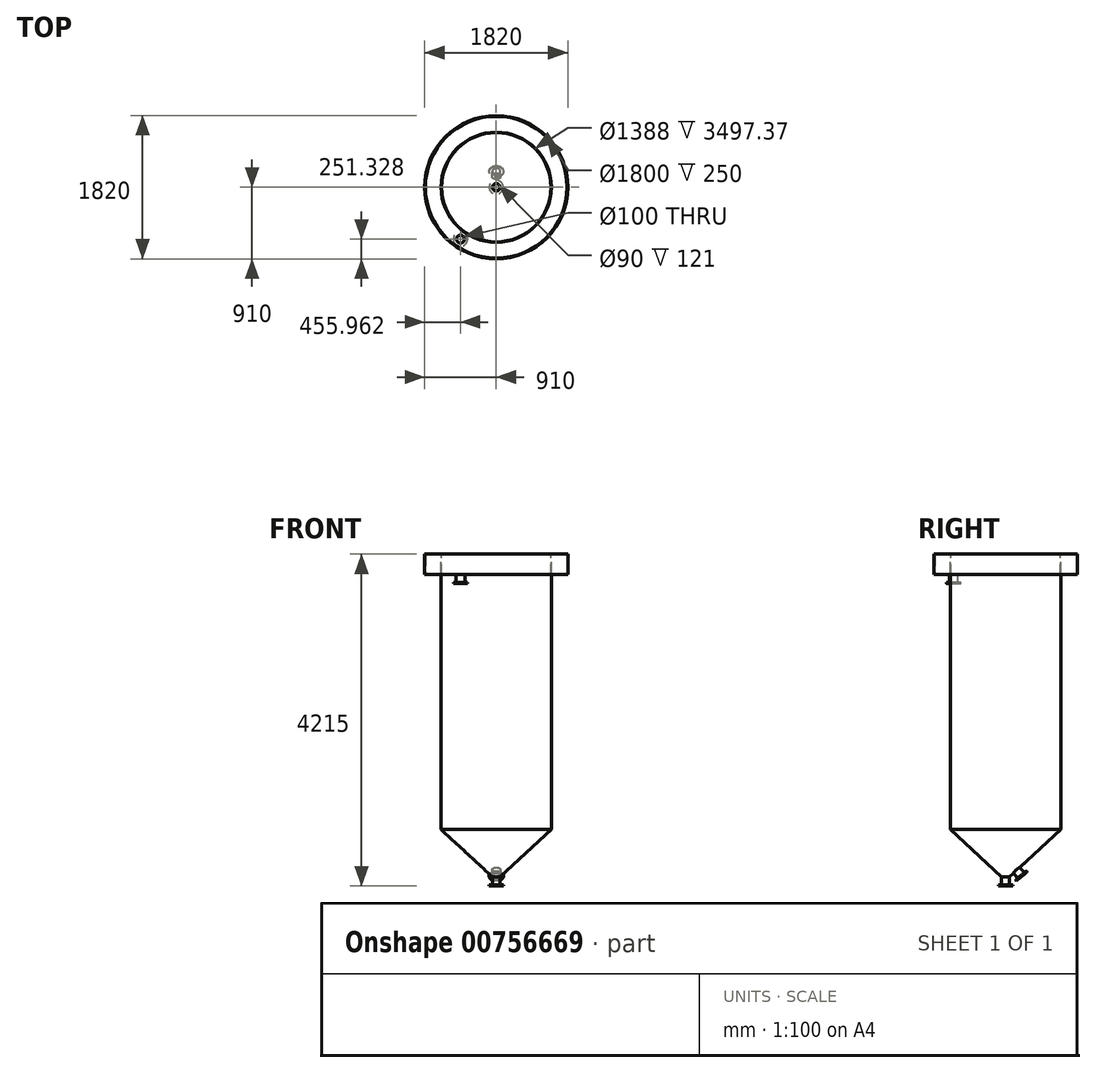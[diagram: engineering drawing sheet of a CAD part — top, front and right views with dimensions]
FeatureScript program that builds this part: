
annotation { "Feature Type Name" : "Feature", "Feature Type Description" : "" }
export const myFeature = defineFeature(function(context is Context, id is Id, definition is map)
    precondition{}
    {
        {
            var Q0;
            Q0=qCreatedBy(makeId("Top.planeOp"),FACE);
            var sketch = newSketch(context, id + "F0", { "sketchPlane" : qUnion([Q0])});
            skCircle(sketch, "E0", {"center": v(0, 0) * mm, "radius": 700 * mm});
            skSolve(sketch);
        }
        {
            var Q0;
            Q0 = qSketchRegion(id + "F0", true);
            extrude(context, id + "F1", {"entities" : qUnion([Q0]), "oppositeDirection" : true, "depth" : 3500 * mm, "offsetDistance" : 25 * mm});
        }
        {
            var Q0;
            Q0=makeQuery(id+"F1.opExtrude","CAP_FACE",FACE,{"disambiguationData":[OSD([sQuery(id+"F0.wireOp",EDGE,"E0")])],"isStart":false});
            var sketch = newSketch(context, id + "F2", { "sketchPlane" : qUnion([Q0])});
            skCircle(sketch, "E1", {"center": v(0, 0) * mm, "radius": 700 * mm});
            skSolve(sketch);
        }
        {
            var Q0;
            Q0 = qSketchRegion(id + "F2", true);
            extrude(context, id + "F3", {"entities" : qUnion([Q0]), "operationType" : NewBodyOperationType.ADD, "depth" : 600 * mm, "offsetDistance" : 25 * mm, "hasDraft" : true, "draftAngle" : 47.3 * degree, "draftPullDirection" : true});
        }
        {
            var Q0;
            Q0=makeQuery(id+"F1.opExtrude","CAP_FACE",FACE,{"disambiguationData":[OSD([sQuery(id+"F0.wireOp",EDGE,"E0")])],"isStart":true});
            shell(context, id + "F4", {"entities" : qUnion([Q0]), "thickness" : 6 * mm});
        }
        {
            var Q0;
            Q0=qCreatedBy(makeId("Front.planeOp"),FACE);
            var sketch = newSketch(context, id + "F5", { "sketchPlane" : qUnion([Q0])});
            skLineSegment(sketch, "E2", {"start": v(0, 0) * mm, "end": v(-700, 0) * mm, "construction": true});
            skLineSegment(sketch, "E3", {"start": v(-700, 0) * mm, "end": v(-700, -250) * mm, "construction": true});
            skLineSegment(sketch, "E4", {"start": v(-700, -250) * mm, "end": v(-700, -260) * mm});
            skLineSegment(sketch, "E5", {"start": v(-700, -260) * mm, "end": v(-910, -260) * mm});
            skLineSegment(sketch, "E6", {"start": v(-910, -260) * mm, "end": v(-910, 0) * mm});
            skLineSegment(sketch, "E7", {"start": v(-910, 0) * mm, "end": v(-900, 0) * mm});
            skLineSegment(sketch, "E8", {"start": v(-900, 0) * mm, "end": v(-900, -250) * mm});
            skLineSegment(sketch, "E9", {"start": v(-900, -250) * mm, "end": v(-700, -250) * mm});
            skSolve(sketch);
        }
        {
            var Q0;
            Q0=qCreatedBy(makeId("Front.planeOp"),FACE);
            var sketch = newSketch(context, id + "F6", { "sketchPlane" : qUnion([Q0])});
            skLineSegment(sketch, "E10", {"start": v(0, 0) * mm, "end": v(0, 82.26) * mm, "construction": true});
            skSolve(sketch);
        }
        {
            var Q0;
            Q0=makeQuery(id+"F5.imprint","IMPRINT",FACE,{"disambiguationData":[TD([[makeQuery(id+"F5.imprint","IMPRINT",EDGE,{"derivedFrom":sQuery(id+"F5.wireOp",EDGE,"E4")}),-1.0]])]});
            var Q1;
            Q1=sQuery(id+"F6.wireOp",EDGE,"E10");
            revolve(context, id + "F7", {"operationType" : NewBodyOperationType.ADD, "surfaceOperationType" : NewSurfaceOperationType.NEW, "entities" : qUnion([Q0]), "axis" : qUnion([Q1]), "revolveType" : RevolveType.FULL});
        }
        {
            var Q0;
            Q0=makeQuery(id+"F7.opRevolve","SWEPT_FACE",FACE,{"disambiguationData":[OSD([sQuery(id+"F5.wireOp",EDGE,"E5")])]});
            var sketch = newSketch(context, id + "F8", { "sketchPlane" : qUnion([Q0])});
            skCircle(sketch, "E11", {"center": v(-454.04, 658.67) * mm, "radius": 50 * mm});
            skSolve(sketch);
        }
        {
            var Q0;
            Q0 = qSketchRegion(id + "F8", true);
            extrude(context, id + "F9", {"entities" : qUnion([Q0]), "operationType" : NewBodyOperationType.REMOVE, "endBound" : BoundingType.THROUGH_ALL, "oppositeDirection" : true, "depth" : 25 * mm, "offsetDistance" : 25 * mm});
        }
        {
            var Q0;
            Q0=makeQuery(id+"F7.opRevolve","SWEPT_FACE",FACE,{"disambiguationData":[OSD([sQuery(id+"F5.wireOp",EDGE,"E5")])]});
            var sketch = newSketch(context, id + "F10", { "sketchPlane" : qUnion([Q0])});
            skCircle(sketch, "E12", {"center": v(-454.04, 658.67) * mm, "radius": 55 * mm});
            skCircle(sketch, "E13", {"center": v(-454.04, 658.67) * mm, "radius": 50 * mm});
            skSolve(sketch);
        }
        {
            var Q0;
            Q0 = qSketchRegion(id + "F10", true);
            extrude(context, id + "F11", {"entities" : qUnion([Q0]), "operationType" : NewBodyOperationType.ADD, "depth" : 100 * mm, "offsetDistance" : 25 * mm});
        }
        {
            var Q0;
            Q0=makeQuery(id+"F11.opExtrude","CAP_FACE",FACE,{"disambiguationData":[OSD([sQuery(id+"F10.wireOp",EDGE,"E12"),sQuery(id+"F10.wireOp",EDGE,"E13")])],"isStart":false});
            var sketch = newSketch(context, id + "F12", { "sketchPlane" : qUnion([Q0])});
            skCircle(sketch, "E14", {"center": v(-454.04, 658.67) * mm, "radius": 50 * mm});
            skCircle(sketch, "E15", {"center": v(-454.04, 658.67) * mm, "radius": 90 * mm});
            skSolve(sketch);
        }
        {
            var Q0;
            Q0 = qSketchRegion(id + "F12", true);
            extrude(context, id + "F13", {"entities" : qUnion([Q0]), "operationType" : NewBodyOperationType.ADD, "depth" : 15 * mm, "offsetDistance" : 25 * mm});
        }
        {
            var Q0;
            Q0=makeQuery(id+"F3.opExtrude","CAP_FACE",FACE,{"disambiguationData":[OSD([sQuery(id+"F2.wireOp",EDGE,"E1")])],"isStart":false});
            var sketch = newSketch(context, id + "F14", { "sketchPlane" : qUnion([Q0])});
            skCircle(sketch, "E16", {"center": v(0, 0) * mm, "radius": 45 * mm});
            skLineSegment(sketch, "E17", {"start": v(0, 0) * mm, "end": v(0, -58) * mm, "construction": true});
            skLineSegment(sketch, "E18", {"start": v(0, -50) * mm, "end": v(35.31, -50) * mm, "construction": true});
            skSolve(sketch);
        }
        {
            var Q0;
            Q0 = qSketchRegion(id + "F14", true);
            extrude(context, id + "F15", {"entities" : qUnion([Q0]), "operationType" : NewBodyOperationType.REMOVE, "oppositeDirection" : true, "depth" : 10 * mm, "offsetDistance" : 25 * mm});
        }
        {
            var Q0;
            Q0=makeQuery(id+"F3.opExtrude","CAP_FACE",FACE,{"disambiguationData":[OSD([sQuery(id+"F2.wireOp",EDGE,"E1")])],"isStart":false});
            var sketch = newSketch(context, id + "F16", { "sketchPlane" : qUnion([Q0])});
            skCircle(sketch, "E19", {"center": v(0, 0) * mm, "radius": 45 * mm});
            skCircle(sketch, "E20", {"center": v(0, 0) * mm, "radius": 50 * mm});
            skSolve(sketch);
        }
        {
            var Q0;
            Q0 = qSketchRegion(id + "F16", true);
            extrude(context, id + "F17", {"entities" : qUnion([Q0]), "operationType" : NewBodyOperationType.ADD, "depth" : 100 * mm, "offsetDistance" : 25 * mm});
        }
        {
            var Q0;
            Q0=makeQuery(id+"F17.opExtrude","CAP_FACE",FACE,{"disambiguationData":[OSD([sQuery(id+"F16.wireOp",EDGE,"E19"),sQuery(id+"F16.wireOp",EDGE,"E20")])],"isStart":false});
            var sketch = newSketch(context, id + "F18", { "sketchPlane" : qUnion([Q0])});
            skCircle(sketch, "E21", {"center": v(0, 0) * mm, "radius": 45 * mm});
            skCircle(sketch, "E22", {"center": v(0, 0) * mm, "radius": 90 * mm});
            skSolve(sketch);
        }
        {
            var Q0;
            Q0 = qSketchRegion(id + "F18", true);
            extrude(context, id + "F19", {"entities" : qUnion([Q0]), "operationType" : NewBodyOperationType.ADD, "depth" : 15 * mm, "offsetDistance" : 25 * mm});
        }
        {
            var Q0;
            Q0=makeQuery(id+"F14.imprint","IMPRINT",FACE,{"disambiguationData":[TD([[makeQuery(id+"F14.imprint","IMPRINT",EDGE,{"derivedFrom":sQuery(id+"F14.wireOp",EDGE,"E16")}),-1.0]])]});
            var Q1;
            Q1=sQuery(id+"F14.wireOp",EDGE,"E18");
            cPlane(context, id + "F20", {"entities" : qUnion([Q0, Q1]), "cplaneType" : CPlaneType.LINE_ANGLE, "offset" : 25 * mm, "angle" : 40 * degree, "width" : 150 * mm, "height" : 150 * mm});
        }
        {
            var Q0;
            Q0=qCreatedBy(id+"F20.planeOp",FACE);
            var sketch = newSketch(context, id + "F21", { "sketchPlane" : qUnion([Q0])});
            skCircle(sketch, "E23", {"center": v(0.59, -2474.47) * mm, "radius": 55 * mm});
            skCircle(sketch, "E24", {"center": v(0.59, -2474.47) * mm, "radius": 50 * mm});
            skSolve(sketch);
        }
        {
            var Q0;
            Q0 = qSketchRegion(id + "F21", true);
            var Q1;
            Q1=makeQuery(id+"F3.opExtrude","SWEPT_FACE",FACE,{"disambiguationData":[OSD([sQuery(id+"F2.wireOp",EDGE,"E1")])]});
            extrude(context, id + "F22", {"entities" : qUnion([Q0]), "operationType" : NewBodyOperationType.ADD, "endBound" : BoundingType.UP_TO_SURFACE, "depth" : 25 * mm, "endBoundEntityFace" : qUnion([Q1]), "offsetDistance" : 25 * mm, "hasSecondDirection" : true, "secondDirectionOppositeDirection" : true, "secondDirectionDepth" : 80 * mm});
        }
        {
            var Q0;
            Q0=makeQuery(id+"F22.opExtrude","CAP_FACE",FACE,{"disambiguationData":[OSD([sQuery(id+"F21.wireOp",EDGE,"E23"),sQuery(id+"F21.wireOp",EDGE,"E24")])],"isStart":true});
            var sketch = newSketch(context, id + "F23", { "sketchPlane" : qUnion([Q0])});
            skCircle(sketch, "E25", {"center": v(0.59, 2474.47) * mm, "radius": 50 * mm});
            skCircle(sketch, "E26", {"center": v(0.59, 2474.47) * mm, "radius": 90 * mm});
            skSolve(sketch);
        }
        {
            var Q0;
            Q0 = qSketchRegion(id + "F23", true);
            extrude(context, id + "F24", {"entities" : qUnion([Q0]), "operationType" : NewBodyOperationType.ADD, "depth" : 15 * mm, "offsetDistance" : 25 * mm});
        }
    });
